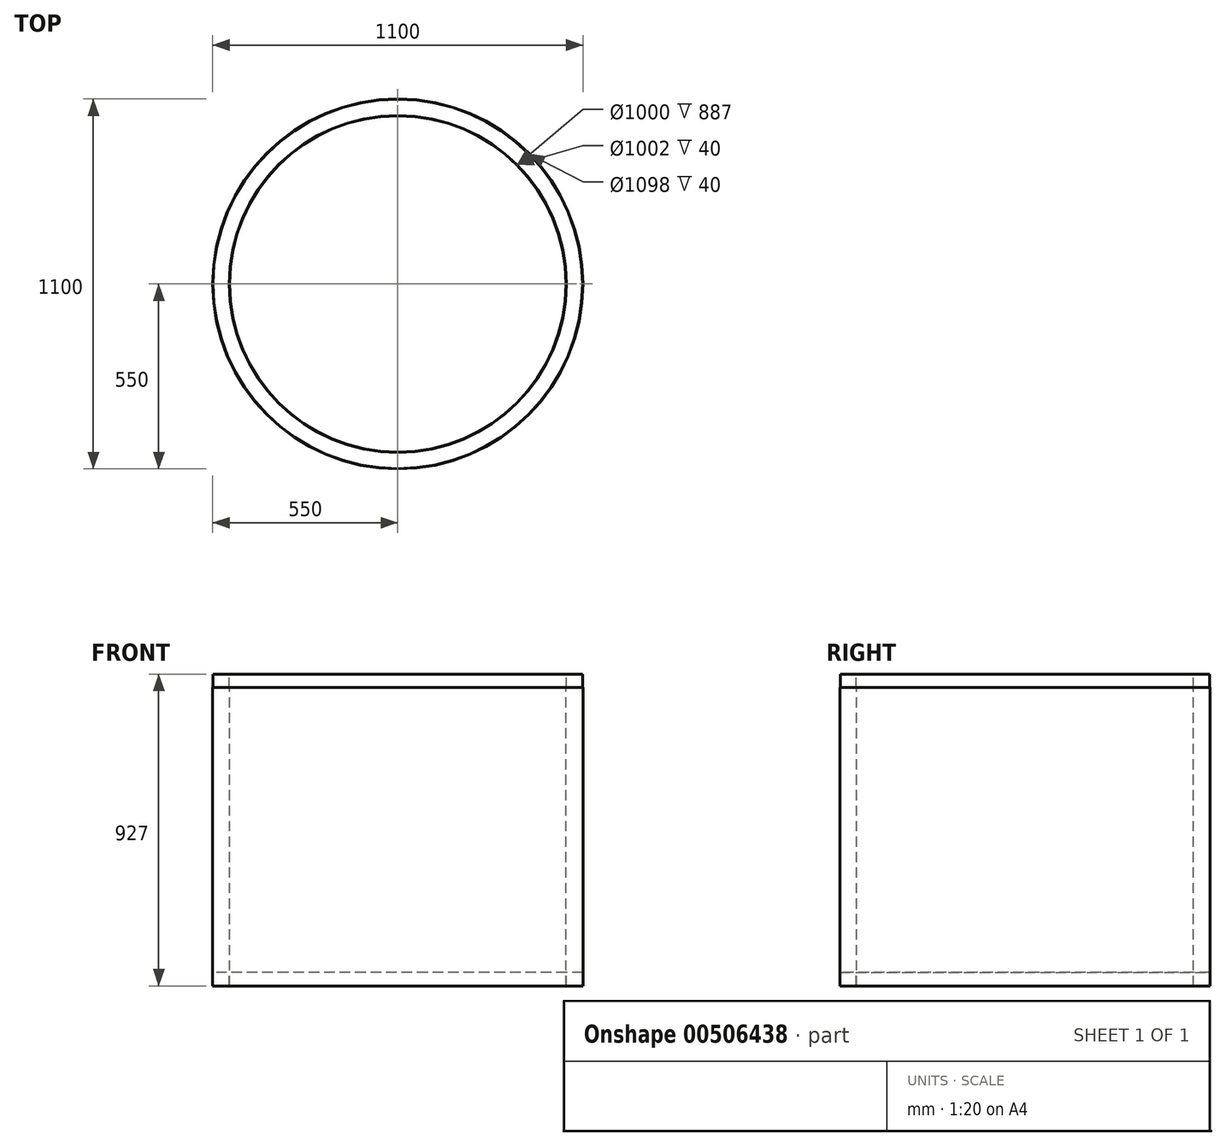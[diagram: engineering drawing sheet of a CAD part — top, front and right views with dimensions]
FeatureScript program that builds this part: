
annotation { "Feature Type Name" : "Feature", "Feature Type Description" : "" }
export const myFeature = defineFeature(function(context is Context, id is Id, definition is map)
    precondition{}
    {
        {
            var Q0;
            Q0=qCreatedBy(makeId("Front.planeOp"),FACE);
            var sketch = newSketch(context, id + "F0", { "sketchPlane" : qUnion([Q0])});
            skLineSegment(sketch, "E0", {"start": v(0, 150.29) * mm, "end": v(0, 1.7) * mm, "construction": true});
            skLineSegment(sketch, "E1", {"start": v(0, 450.26) * mm, "end": v(0, -453.52) * mm, "construction": true});
            skLineSegment(sketch, "E2", {"start": v(-500, -414.33) * mm, "end": v(-500, 472.67) * mm});
            skLineSegment(sketch, "E3", {"start": v(-500, 472.67) * mm, "end": v(-501, 472.67) * mm});
            skLineSegment(sketch, "E4", {"start": v(-501, 472.67) * mm, "end": v(-501, 512.67) * mm});
            skLineSegment(sketch, "E5", {"start": v(-501, 512.67) * mm, "end": v(-549, 512.67) * mm});
            skLineSegment(sketch, "E6", {"start": v(-549, 512.67) * mm, "end": v(-549, 472.67) * mm});
            skLineSegment(sketch, "E7", {"start": v(-549, 472.67) * mm, "end": v(-550, 472.67) * mm});
            skLineSegment(sketch, "E8", {"start": v(-550, 472.67) * mm, "end": v(-550, -414.33) * mm});
            skLineSegment(sketch, "E9", {"start": v(-550, -414.33) * mm, "end": v(-549, -414.33) * mm});
            skLineSegment(sketch, "E10", {"start": v(-549, -414.33) * mm, "end": v(-549, -374.33) * mm});
            skLineSegment(sketch, "E11", {"start": v(-549, -374.33) * mm, "end": v(-501, -374.33) * mm});
            skLineSegment(sketch, "E12", {"start": v(-501, -374.33) * mm, "end": v(-501, -414.33) * mm});
            skLineSegment(sketch, "E13", {"start": v(-501, -414.33) * mm, "end": v(-500, -414.33) * mm});
            skSolve(sketch);
        }
        {
            var Q0;
            Q0=qSketchRegion(id+"F0",true);
            var Q1;
            Q1=sQuery(id+"F0.wireOp",EDGE,"E1");
            revolve(context, id + "F1", {"entities" : qUnion([Q0]), "axis" : qUnion([Q1]), "revolveType" : RevolveType.FULL});
        }
    });
